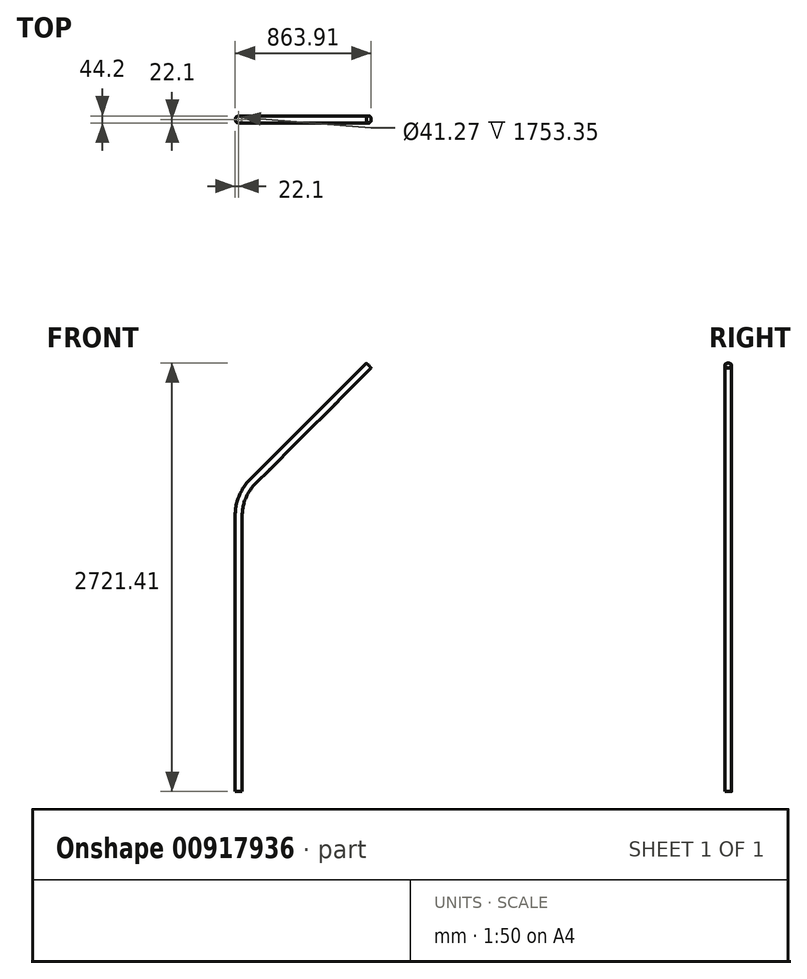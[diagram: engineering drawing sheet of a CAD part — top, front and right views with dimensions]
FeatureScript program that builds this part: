
annotation { "Feature Type Name" : "Feature", "Feature Type Description" : "" }
export const myFeature = defineFeature(function(context is Context, id is Id, definition is map)
    precondition{}
    {
        {
            var Q0;
            Q0=qCreatedBy(makeId("Top.planeOp"),FACE);
            var sketch = newSketch(context, id + "F0", { "sketchPlane" : qUnion([Q0])});
            skCircle(sketch, "E0", {"center": v(0, 0) * mm, "radius": 22.1 * mm});
            skSolve(sketch);
        }
        {
            var Q0;
            Q0=qCreatedBy(makeId("Front.planeOp"),FACE);
            var sketch = newSketch(context, id + "F1", { "sketchPlane" : qUnion([Q0])});
            skLineSegment(sketch, "E1", {"start": v(0, 0) * mm, "end": v(0, 1753.35) * mm});
            skLineSegment(sketch, "E2", {"start": v(89.27, 1968.87) * mm, "end": v(826.18, 2705.78) * mm});
            skPoint(sketch, "E3.visualSharp", {"position": v(0, 1879.6) * mm});
            skArc(sketch, "E3.filletArc", {"start": v(89.27, 1968.87) * mm, "mid": v(23.2, 1869.99) * mm, "end": v(0, 1753.35) * mm});
            skSolve(sketch);
        }
        {
            var Q0;
            Q0=makeQuery(id+"F0.imprint","IMPRINT",FACE,{"disambiguationData":[TD([[makeQuery(id+"F0.imprint","IMPRINT",EDGE,{"derivedFrom":sQuery(id+"F0.wireOp",EDGE,"E0")}),1.0]])]});
            var Q1;
            Q1=sQuery(id+"F1.wireOp",EDGE,"E2");
            var Q2;
            Q2=sQuery(id+"F1.wireOp",EDGE,"E1");
            var Q3;
            Q3=sQuery(id+"F1.wireOp",EDGE,"E3.filletArc");
            sweep(context, id + "F2", {"profiles" : qUnion([Q0]), "surfaceOperationType" : NewSurfaceOperationType.ADD, "path" : qUnion([Q1, Q2, Q3])});
        }
        {
            var Q0;
            Q0=makeQuery(id+"F0.imprint","IMPRINT",FACE,{"disambiguationData":[TD([[makeQuery(id+"F0.imprint","IMPRINT",EDGE,{"derivedFrom":sQuery(id+"F0.wireOp",EDGE,"E0")}),1.0]])]});
            var sketch = newSketch(context, id + "F3", { "sketchPlane" : qUnion([Q0])});
            skCircle(sketch, "E4", {"center": v(0, 0) * mm, "radius": 20.64 * mm});
            skSolve(sketch);
        }
        {
            var Q0;
            Q0 = qSketchRegion(id + "F3", true);
            var Q1;
            Q1=sQuery(id+"F1.wireOp",EDGE,"E1");
            var Q2;
            Q2=sQuery(id+"F1.wireOp",EDGE,"E3.filletArc");
            var Q3;
            Q3=sQuery(id+"F1.wireOp",EDGE,"E2");
            sweep(context, id + "F4", {"operationType" : NewBodyOperationType.REMOVE, "profiles" : qUnion([Q0]), "path" : qUnion([Q1, Q2, Q3])});
        }
    });
